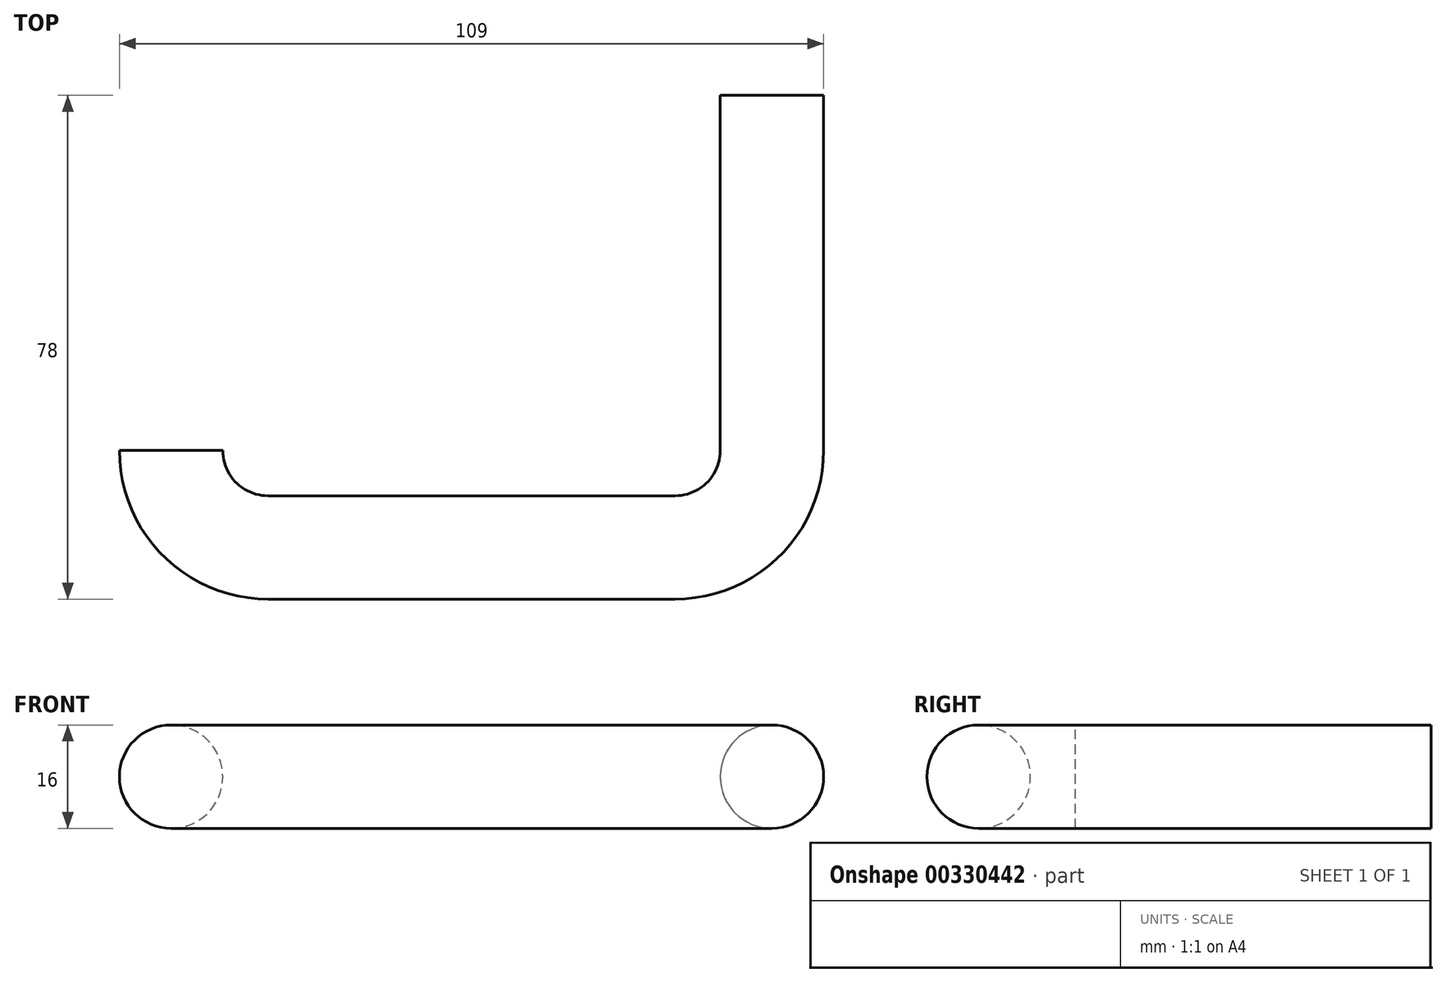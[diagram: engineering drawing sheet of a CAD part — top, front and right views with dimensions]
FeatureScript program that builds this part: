
annotation { "Feature Type Name" : "Feature", "Feature Type Description" : "" }
export const myFeature = defineFeature(function(context is Context, id is Id, definition is map)
    precondition{}
    {
        {
            var Q0;
            Q0=qCreatedBy(makeId("Front.planeOp"),FACE);
            var sketch = newSketch(context, id + "F0", { "sketchPlane" : qUnion([Q0])});
            skCircle(sketch, "E0", {"center": v(0, 0) * mm, "radius": 8 * mm});
            skSolve(sketch);
        }
        {
            var Q0;
            Q0=qCreatedBy(makeId("Top.planeOp"),FACE);
            var sketch = newSketch(context, id + "F1", { "sketchPlane" : qUnion([Q0])});
            skLineSegment(sketch, "E1", {"start": v(0, 0) * mm, "end": v(0, 0) * mm});
            skLineSegment(sketch, "E2", {"start": v(15, -15) * mm, "end": v(78, -15) * mm});
            skLineSegment(sketch, "E3", {"start": v(93, 0) * mm, "end": v(93, 55) * mm});
            skPoint(sketch, "E4.visualSharp", {"position": v(0, -15) * mm});
            skArc(sketch, "E4.filletArc", {"start": v(0, 0) * mm, "mid": v(4.4, -10.6) * mm, "end": v(15, -15) * mm});
            skPoint(sketch, "E5.visualSharp", {"position": v(93, -15) * mm});
            skArc(sketch, "E5.filletArc", {"start": v(78, -15) * mm, "mid": v(88.6, -10.6) * mm, "end": v(93, 0) * mm});
            skSolve(sketch);
        }
        {
            var Q0;
            Q0=makeQuery(id+"F0.imprint","IMPRINT",FACE,{"disambiguationData":[TD([[makeQuery(id+"F0.imprint","IMPRINT",EDGE,{"derivedFrom":sQuery(id+"F0.wireOp",EDGE,"E0")}),1.0]])]});
            var Q1;
            Q1=sQuery(id+"F1.wireOp",EDGE,"E4.filletArc");
            var Q2;
            Q2=sQuery(id+"F1.wireOp",EDGE,"E2");
            var Q3;
            Q3=sQuery(id+"F1.wireOp",EDGE,"E5.filletArc");
            var Q4;
            Q4=sQuery(id+"F1.wireOp",EDGE,"E3");
            sweep(context, id + "F2", {"profiles" : qUnion([Q0]), "path" : qUnion([Q1, Q2, Q3, Q4])});
        }
    });
